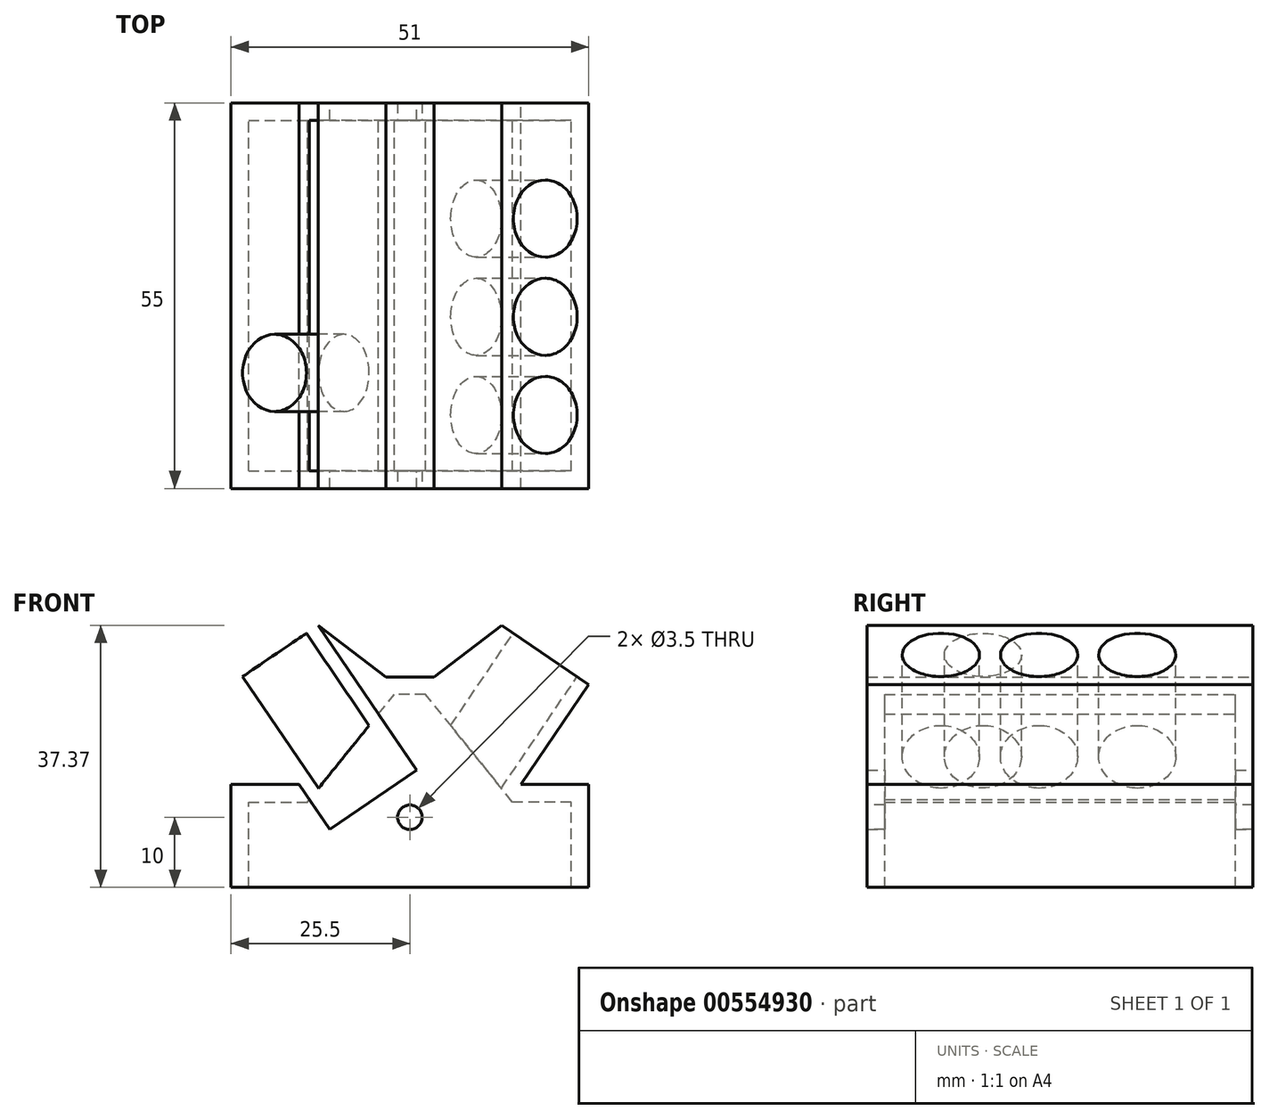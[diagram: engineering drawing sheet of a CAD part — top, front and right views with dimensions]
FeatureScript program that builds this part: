
annotation { "Feature Type Name" : "Feature", "Feature Type Description" : "" }
export const myFeature = defineFeature(function(context is Context, id is Id, definition is map)
    precondition{}
    {
        {
            var Q0;
            Q0=qCreatedBy(makeId("Front.planeOp"),FACE);
            var sketch = newSketch(context, id + "F0", { "sketchPlane" : qUnion([Q0])});
            skLineSegment(sketch, "E0", {"start": v(0, 0) * mm, "end": v(-25.5, 0) * mm});
            skLineSegment(sketch, "E1", {"start": v(-25.5, 0) * mm, "end": v(-25.5, 14.68) * mm});
            skLineSegment(sketch, "E2", {"start": v(-25.5, 14.68) * mm, "end": v(-15.81, 14.68) * mm});
            skLineSegment(sketch, "E3", {"start": v(-15.81, 14.68) * mm, "end": v(-25.5, 28.95) * mm});
            skLineSegment(sketch, "E4", {"start": v(-25.5, 28.95) * mm, "end": v(-13.1, 37.37) * mm});
            skLineSegment(sketch, "E5", {"start": v(-13.1, 37.37) * mm, "end": v(-3.43, 30.02) * mm});
            skLineSegment(sketch, "E6", {"start": v(-3.43, 30.02) * mm, "end": v(0, 30.02) * mm});
            skLineSegment(sketch, "E7", {"start": v(0, 30.02) * mm, "end": v(0, 0) * mm});
            skLineSegment(sketch, "E8.MirrorCS", {"start": v(3.43, 30.02) * mm, "end": v(0, 30.02) * mm});
            skLineSegment(sketch, "E9.MirrorCS", {"start": v(13.1, 37.37) * mm, "end": v(3.43, 30.02) * mm});
            skLineSegment(sketch, "E10.MirrorCS", {"start": v(25.5, 28.95) * mm, "end": v(13.1, 37.37) * mm});
            skLineSegment(sketch, "E11.MirrorCS", {"start": v(25.5, 14.68) * mm, "end": v(15.81, 14.68) * mm});
            skLineSegment(sketch, "E12.MirrorCS", {"start": v(0, 0) * mm, "end": v(25.5, 0) * mm});
            skLineSegment(sketch, "E13.MirrorCS", {"start": v(15.81, 14.68) * mm, "end": v(25.5, 28.95) * mm});
            skLineSegment(sketch, "E14.MirrorCS", {"start": v(25.5, 0) * mm, "end": v(25.5, 14.68) * mm});
            skPoint(sketch, "E15", {"position": v(0, 10) * mm});
            skLineSegment(sketch, "E16", {"start": v(15.81, 14.68) * mm, "end": v(3.43, 30.02) * mm});
            skLineSegment(sketch, "E17", {"start": v(-15.81, 14.68) * mm, "end": v(-3.43, 30.02) * mm});
            skSolve(sketch);
        }
        {
            var Q0;
            Q0=makeQuery(id+"F0.imprint","IMPRINT",FACE,{"disambiguationData":[TD([[makeQuery(id+"F0.imprint","IMPRINT",EDGE,{"derivedFrom":sQuery(id+"F0.wireOp",EDGE,"E7")}),1.0]])]});
            var Q1;
            Q1=makeQuery(id+"F0.imprint","IMPRINT",FACE,{"disambiguationData":[TD([[makeQuery(id+"F0.imprint","IMPRINT",EDGE,{"derivedFrom":sQuery(id+"F0.wireOp",EDGE,"E0")}),-1.0]])]});
            extrude(context, id + "F1", {"entities" : qUnion([Q0, Q1]), "depth" : 55 * mm, "offsetDistance" : 25 * mm});
        }
        {
            var Q0;
            Q0=makeQuery(id+"F1.opExtrude","SWEPT_FACE",FACE,{"disambiguationData":[OSD([sQuery(id+"F0.wireOp",EDGE,"E0"),sQuery(id+"F0.wireOp",EDGE,"E12.MirrorCS")])]});
            shell(context, id + "F2", {"entities" : qUnion([Q0]), "thickness" : 2.5 * mm});
        }
        {
            var Q0;
            Q0=makeQuery(id+"F0.imprint","IMPRINT",FACE,{"disambiguationData":[TD([[makeQuery(id+"F0.imprint","IMPRINT",EDGE,{"derivedFrom":sQuery(id+"F0.wireOp",EDGE,"E9.MirrorCS")}),1.0]])]});
            var Q1;
            Q1=makeQuery(id+"F0.imprint","IMPRINT",FACE,{"disambiguationData":[TD([[makeQuery(id+"F0.imprint","IMPRINT",EDGE,{"derivedFrom":sQuery(id+"F0.wireOp",EDGE,"E3")}),-1.0]])]});
            extrude(context, id + "F3", {"entities" : qUnion([Q0, Q1]), "operationType" : NewBodyOperationType.ADD, "depth" : 55 * mm, "offsetDistance" : 25 * mm});
        }
        {
            var Q0;
            Q0=makeQuery(id+"F3.opExtrude","SWEPT_FACE",FACE,{"disambiguationData":[OSD([sQuery(id+"F0.wireOp",EDGE,"E10.MirrorCS")])]});
            var sketch = newSketch(context, id + "F4", { "sketchPlane" : qUnion([Q0])});
            skLineSegment(sketch, "E18.0", {"start": v(-10.17, -55) * mm, "end": v(-10.17, 0) * mm});
            skLineSegment(sketch, "E19.0", {"start": v(4.83, -55) * mm, "end": v(-10.17, -55) * mm});
            skLineSegment(sketch, "E20.0", {"start": v(4.83, -55) * mm, "end": v(4.83, 0) * mm});
            skLineSegment(sketch, "E21.0", {"start": v(4.83, 0) * mm, "end": v(-10.17, 0) * mm});
            skLineSegment(sketch, "E22", {"start": v(-2.67, -55) * mm, "end": v(-2.67, 0) * mm});
            skCircle(sketch, "E23", {"center": v(-2.67, -44.5) * mm, "radius": 5.5 * mm});
            skCircle(sketch, "E24", {"center": v(-2.67, -30.5) * mm, "radius": 5.5 * mm});
            skCircle(sketch, "E25", {"center": v(-2.67, -16.5) * mm, "radius": 5.5 * mm});
            skSolve(sketch);
        }
        {
            var Q0;
            {var subQ0=sQuery(id+"F4.wireOp",EDGE,"E23");var subQ1=sQuery(id+"F4.wireOp",EDGE,"E22");var subQ2=makeQuery(id+"F4.imprint","INTERSECT",VERTEX,{"disambiguationData":[OD(0.0)],"derivedFrom":[subQ1,subQ0]});Q0=makeQuery(id+"F4.imprint","IMPRINT",FACE,{"disambiguationData":[TD([[makeQuery(id+"F4.imprint","IMPRINT",EDGE,{"disambiguationData":[TD([[subQ2,-1.0]])],"derivedFrom":subQ1}),1.0]])]});}
            var Q1;
            {var subQ0=sQuery(id+"F4.wireOp",EDGE,"E23");var subQ1=sQuery(id+"F4.wireOp",EDGE,"E22");var subQ2=makeQuery(id+"F4.imprint","INTERSECT",VERTEX,{"disambiguationData":[OD(0.0)],"derivedFrom":[subQ1,subQ0]});Q1=makeQuery(id+"F4.imprint","IMPRINT",FACE,{"disambiguationData":[TD([[makeQuery(id+"F4.imprint","IMPRINT",EDGE,{"disambiguationData":[TD([[subQ2,-1.0]])],"derivedFrom":subQ1}),-1.0]])]});}
            var Q2;
            {var subQ0=sQuery(id+"F4.wireOp",EDGE,"E24");var subQ1=sQuery(id+"F4.wireOp",EDGE,"E22");var subQ2=makeQuery(id+"F4.imprint","INTERSECT",VERTEX,{"disambiguationData":[OD(0.0)],"derivedFrom":[subQ1,subQ0]});Q2=makeQuery(id+"F4.imprint","IMPRINT",FACE,{"disambiguationData":[TD([[makeQuery(id+"F4.imprint","IMPRINT",EDGE,{"disambiguationData":[TD([[subQ2,-1.0]])],"derivedFrom":subQ1}),1.0]])]});}
            var Q3;
            {var subQ0=sQuery(id+"F4.wireOp",EDGE,"E24");var subQ1=sQuery(id+"F4.wireOp",EDGE,"E22");var subQ2=makeQuery(id+"F4.imprint","INTERSECT",VERTEX,{"disambiguationData":[OD(0.0)],"derivedFrom":[subQ1,subQ0]});Q3=makeQuery(id+"F4.imprint","IMPRINT",FACE,{"disambiguationData":[TD([[makeQuery(id+"F4.imprint","IMPRINT",EDGE,{"disambiguationData":[TD([[subQ2,-1.0]])],"derivedFrom":subQ1}),-1.0]])]});}
            var Q4;
            {var subQ0=sQuery(id+"F4.wireOp",EDGE,"E25");var subQ1=sQuery(id+"F4.wireOp",EDGE,"E22");var subQ2=makeQuery(id+"F4.imprint","INTERSECT",VERTEX,{"disambiguationData":[OD(0.0)],"derivedFrom":[subQ1,subQ0]});Q4=makeQuery(id+"F4.imprint","IMPRINT",FACE,{"disambiguationData":[TD([[makeQuery(id+"F4.imprint","IMPRINT",EDGE,{"disambiguationData":[TD([[subQ2,-1.0]])],"derivedFrom":subQ1}),1.0]])]});}
            var Q5;
            {var subQ0=sQuery(id+"F4.wireOp",EDGE,"E25");var subQ1=sQuery(id+"F4.wireOp",EDGE,"E22");var subQ2=makeQuery(id+"F4.imprint","INTERSECT",VERTEX,{"disambiguationData":[OD(0.0)],"derivedFrom":[subQ1,subQ0]});Q5=makeQuery(id+"F4.imprint","IMPRINT",FACE,{"disambiguationData":[TD([[makeQuery(id+"F4.imprint","IMPRINT",EDGE,{"disambiguationData":[TD([[subQ2,-1.0]])],"derivedFrom":subQ1}),-1.0]])]});}
            extrude(context, id + "F5", {"entities" : qUnion([Q0, Q1, Q2, Q3, Q4, Q5]), "operationType" : NewBodyOperationType.REMOVE, "oppositeDirection" : true, "depth" : 25 * mm, "offsetDistance" : 25 * mm});
        }
        {
            var Q0;
            Q0=makeQuery(id+"F3.opExtrude","SWEPT_FACE",FACE,{"disambiguationData":[OSD([sQuery(id+"F0.wireOp",EDGE,"E4")])]});
            var sketch = newSketch(context, id + "F6", { "sketchPlane" : qUnion([Q0])});
            skLineSegment(sketch, "E26.0.0", {"start": v(10.17, 0) * mm, "end": v(-4.83, 0) * mm});
            skLineSegment(sketch, "E26.0.1", {"start": v(-4.83, 0) * mm, "end": v(-4.83, -55) * mm});
            skLineSegment(sketch, "E26.0.2", {"start": v(-4.83, -55) * mm, "end": v(10.17, -55) * mm});
            skLineSegment(sketch, "E26.0.3", {"start": v(10.17, -55) * mm, "end": v(10.17, 0) * mm});
            skLineSegment(sketch, "E27", {"start": v(2.67, 0) * mm, "end": v(2.67, -55) * mm});
            skCircle(sketch, "E28", {"center": v(2.67, -10.5) * mm, "radius": 5.5 * mm});
            skCircle(sketch, "E29", {"center": v(2.67, -24.5) * mm, "radius": 5.5 * mm});
            skCircle(sketch, "E30", {"center": v(2.67, -38.5) * mm, "radius": 5.5 * mm});
            skSolve(sketch);
        }
        {
            var Q0;
            {var subQ0=sQuery(id+"F6.wireOp",EDGE,"E28");var subQ1=sQuery(id+"F6.wireOp",EDGE,"E27");var subQ2=makeQuery(id+"F6.imprint","INTERSECT",VERTEX,{"disambiguationData":[OD(0.0)],"derivedFrom":[subQ1,subQ0]});Q0=makeQuery(id+"F6.imprint","IMPRINT",FACE,{"disambiguationData":[TD([[makeQuery(id+"F6.imprint","IMPRINT",EDGE,{"disambiguationData":[TD([[subQ2,-1.0]])],"derivedFrom":subQ1}),1.0]])]});}
            var Q1;
            {var subQ0=sQuery(id+"F6.wireOp",EDGE,"E28");var subQ1=sQuery(id+"F6.wireOp",EDGE,"E27");var subQ2=makeQuery(id+"F6.imprint","INTERSECT",VERTEX,{"disambiguationData":[OD(0.0)],"derivedFrom":[subQ1,subQ0]});Q1=makeQuery(id+"F6.imprint","IMPRINT",FACE,{"disambiguationData":[TD([[makeQuery(id+"F6.imprint","IMPRINT",EDGE,{"disambiguationData":[TD([[subQ2,-1.0]])],"derivedFrom":subQ1}),-1.0]])]});}
            var Q2;
            {var subQ0=sQuery(id+"F6.wireOp",EDGE,"E29");var subQ1=sQuery(id+"F6.wireOp",EDGE,"E27");var subQ2=makeQuery(id+"F6.imprint","INTERSECT",VERTEX,{"disambiguationData":[OD(0.0)],"derivedFrom":[subQ1,subQ0]});Q2=makeQuery(id+"F6.imprint","IMPRINT",FACE,{"disambiguationData":[TD([[makeQuery(id+"F6.imprint","IMPRINT",EDGE,{"disambiguationData":[TD([[subQ2,-1.0]])],"derivedFrom":subQ1}),1.0]])]});}
            var Q3;
            {var subQ0=sQuery(id+"F6.wireOp",EDGE,"E29");var subQ1=sQuery(id+"F6.wireOp",EDGE,"E27");var subQ2=makeQuery(id+"F6.imprint","INTERSECT",VERTEX,{"disambiguationData":[OD(0.0)],"derivedFrom":[subQ1,subQ0]});Q3=makeQuery(id+"F6.imprint","IMPRINT",FACE,{"disambiguationData":[TD([[makeQuery(id+"F6.imprint","IMPRINT",EDGE,{"disambiguationData":[TD([[subQ2,-1.0]])],"derivedFrom":subQ1}),-1.0]])]});}
            var Q4;
            {var subQ0=sQuery(id+"F6.wireOp",EDGE,"E30");var subQ1=sQuery(id+"F6.wireOp",EDGE,"E27");var subQ2=makeQuery(id+"F6.imprint","INTERSECT",VERTEX,{"disambiguationData":[OD(0.0)],"derivedFrom":[subQ1,subQ0]});Q4=makeQuery(id+"F6.imprint","IMPRINT",FACE,{"disambiguationData":[TD([[makeQuery(id+"F6.imprint","IMPRINT",EDGE,{"disambiguationData":[TD([[subQ2,-1.0]])],"derivedFrom":subQ1}),1.0]])]});}
            var Q5;
            {var subQ0=sQuery(id+"F6.wireOp",EDGE,"E30");var subQ1=sQuery(id+"F6.wireOp",EDGE,"E27");var subQ2=makeQuery(id+"F6.imprint","INTERSECT",VERTEX,{"disambiguationData":[OD(0.0)],"derivedFrom":[subQ1,subQ0]});Q5=makeQuery(id+"F6.imprint","IMPRINT",FACE,{"disambiguationData":[TD([[makeQuery(id+"F6.imprint","IMPRINT",EDGE,{"disambiguationData":[TD([[subQ2,-1.0]])],"derivedFrom":subQ1}),-1.0]])]});}
            extrude(context, id + "F7", {"entities" : qUnion([Q0, Q1, Q2, Q3, Q4, Q5]), "operationType" : NewBodyOperationType.REMOVE, "oppositeDirection" : true, "depth" : 25 * mm, "offsetDistance" : 25 * mm});
        }
        {
            var Q0;
            {var subQ0=sQuery(id+"F0.wireOp",EDGE,"E16");var subQ1=sQuery(id+"F0.wireOp",EDGE,"E17");Q0=makeQuery(id+"F3.boolean.opBoolean","MERGE",FACE,{"derivedFrom":[makeQuery(id+"F1.opExtrude","CAP_FACE",FACE,{"disambiguationData":[OSD([sQuery(id+"F0.wireOp",EDGE,"E0"),sQuery(id+"F0.wireOp",EDGE,"E1"),sQuery(id+"F0.wireOp",EDGE,"E2"),sQuery(id+"F0.wireOp",EDGE,"E6"),sQuery(id+"F0.wireOp",EDGE,"E8.MirrorCS"),sQuery(id+"F0.wireOp",EDGE,"E11.MirrorCS"),sQuery(id+"F0.wireOp",EDGE,"E12.MirrorCS"),sQuery(id+"F0.wireOp",EDGE,"E14.MirrorCS"),subQ0,subQ1])],"isStart":false}),makeQuery(id+"F3.opExtrude","CAP_FACE",FACE,{"disambiguationData":[OSD([sQuery(id+"F0.wireOp",EDGE,"E3"),sQuery(id+"F0.wireOp",EDGE,"E4"),sQuery(id+"F0.wireOp",EDGE,"E5"),subQ1])],"isStart":false}),makeQuery(id+"F3.opExtrude","CAP_FACE",FACE,{"disambiguationData":[OSD([sQuery(id+"F0.wireOp",EDGE,"E9.MirrorCS"),sQuery(id+"F0.wireOp",EDGE,"E10.MirrorCS"),sQuery(id+"F0.wireOp",EDGE,"E13.MirrorCS"),subQ0])],"isStart":false})]});}
            var sketch = newSketch(context, id + "F8", { "sketchPlane" : qUnion([Q0])});
            skPoint(sketch, "E31.0", {"position": v(0, 10) * mm});
            skCircle(sketch, "E32", {"center": v(0, 10) * mm, "radius": 1.75 * mm});
            skSolve(sketch);
        }
        {
            var Q0;
            Q0 = qSketchRegion(id + "F8", true);
            extrude(context, id + "F9", {"entities" : qUnion([Q0]), "operationType" : NewBodyOperationType.REMOVE, "oppositeDirection" : true, "depth" : 60 * mm, "offsetDistance" : 25 * mm});
        }
    });
